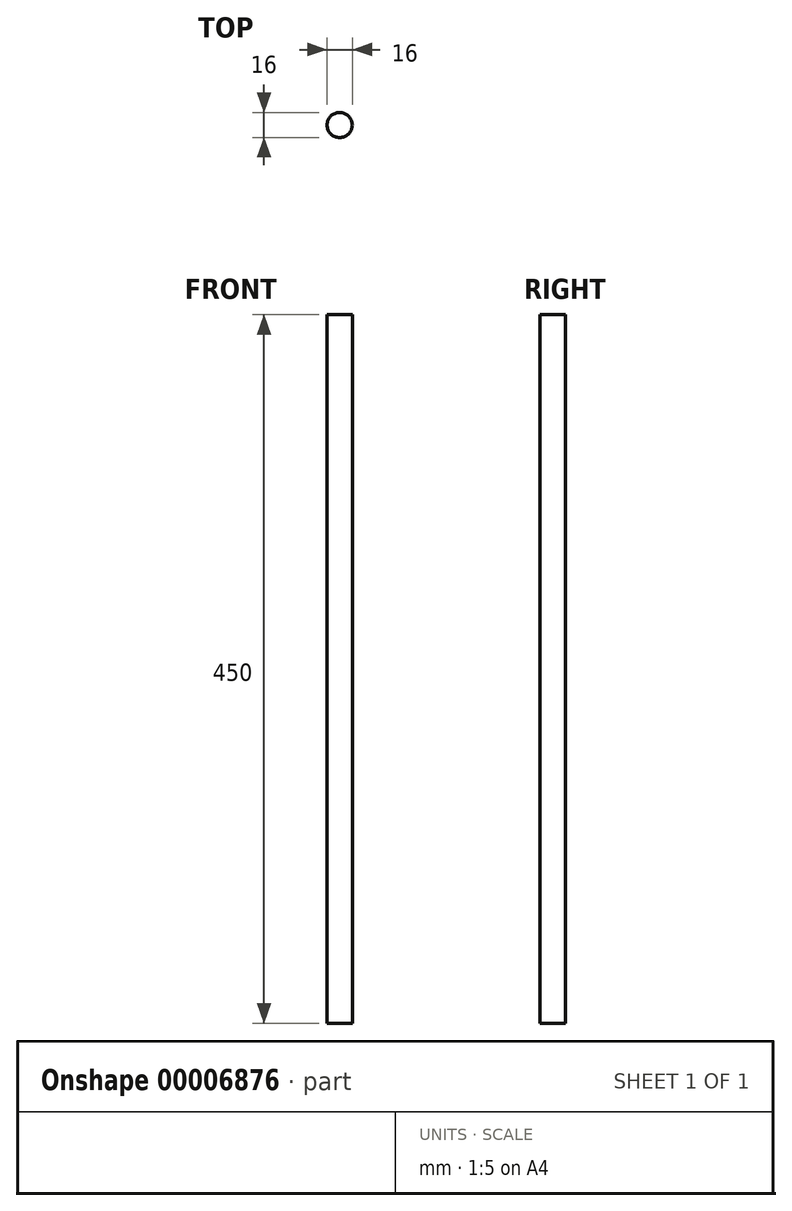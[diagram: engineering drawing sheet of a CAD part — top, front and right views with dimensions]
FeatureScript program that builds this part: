
annotation { "Feature Type Name" : "Feature", "Feature Type Description" : "" }
export const myFeature = defineFeature(function(context is Context, id is Id, definition is map)
    precondition{}
    {
        {
            var Q0;
            Q0=qCreatedBy(makeId("Top.planeOp"),FACE);
            var sketch = newSketch(context, id + "F0", { "sketchPlane" : qUnion([Q0])});
            skCircle(sketch, "E0", {"center": v(0, 0) * mm, "radius": 8 * mm});
            skSolve(sketch);
        }
        {
            var Q0;
            Q0 = qSketchRegion(id + "F0", true);
            extrude(context, id + "F1", {"entities" : qUnion([Q0]), "depth" : (450) * mm});
        }
    });
